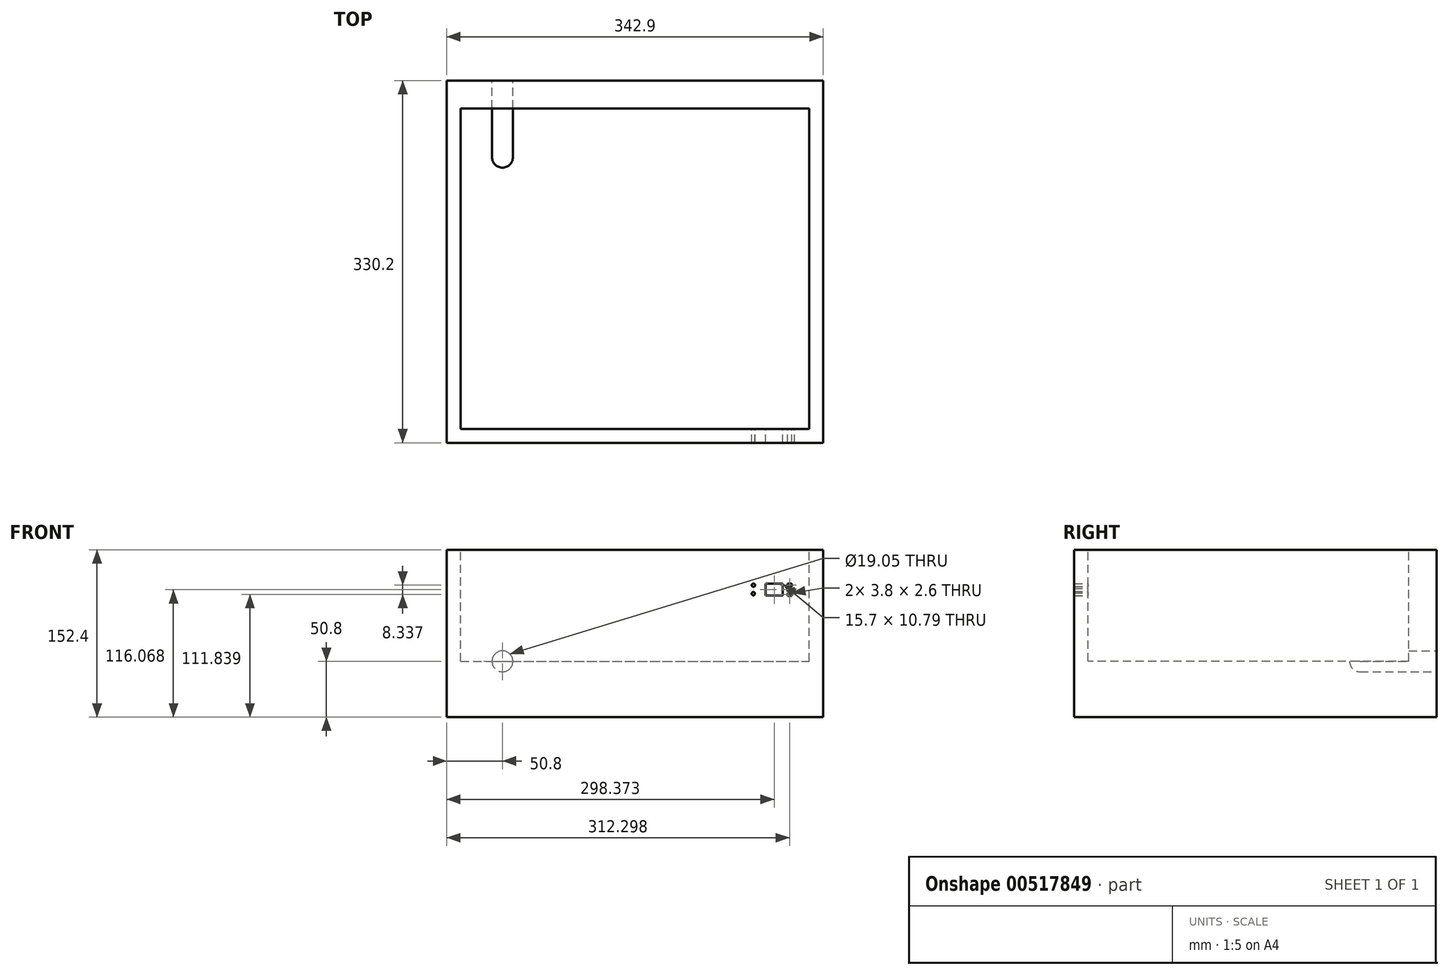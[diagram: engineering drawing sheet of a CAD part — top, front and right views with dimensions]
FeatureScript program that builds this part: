
annotation { "Feature Type Name" : "Feature", "Feature Type Description" : "" }
export const myFeature = defineFeature(function(context is Context, id is Id, definition is map)
    precondition{}
    {
        {
            var Q0;
            Q0=qCreatedBy(makeId("Top.planeOp"),FACE);
            var sketch = newSketch(context, id + "F0", { "sketchPlane" : qUnion([Q0])});
            skLineSegment(sketch, "E0.bottom", {"start": v(171.45, -165.1) * mm, "end": v(-171.45, -165.1) * mm});
            skLineSegment(sketch, "E0.top", {"start": v(171.45, 165.1) * mm, "end": v(-171.45, 165.1) * mm});
            skLineSegment(sketch, "E0.left", {"start": v(171.45, -165.1) * mm, "end": v(171.45, 165.1) * mm});
            skLineSegment(sketch, "E0.right", {"start": v(-171.45, -165.1) * mm, "end": v(-171.45, 165.1) * mm});
            skPoint(sketch, "E0.middle", {"position": v(0, 0) * mm});
            skSolve(sketch);
        }
        {
            var Q0;
            Q0 = qSketchRegion(id + "F0", true);
            extrude(context, id + "F1", {"entities" : qUnion([Q0]), "depth" : 152.4 * mm, "offsetDistance" : 25.4 * mm});
        }
        {
            var Q0;
            Q0=makeQuery(id+"F1.opExtrude","CAP_FACE",FACE,{"disambiguationData":[OSD([sQuery(id+"F0.wireOp",EDGE,"E0.bottom"),sQuery(id+"F0.wireOp",EDGE,"E0.top"),sQuery(id+"F0.wireOp",EDGE,"E0.left"),sQuery(id+"F0.wireOp",EDGE,"E0.right")])],"isStart":false});
            var sketch = newSketch(context, id + "F2", { "sketchPlane" : qUnion([Q0])});
            skLineSegment(sketch, "E1.bottom", {"start": v(-158.75, 139.7) * mm, "end": v(158.75, 139.7) * mm});
            skLineSegment(sketch, "E1.top", {"start": v(-158.75, -152.4) * mm, "end": v(158.75, -152.4) * mm});
            skLineSegment(sketch, "E1.left", {"start": v(-158.75, 139.7) * mm, "end": v(-158.75, -152.4) * mm});
            skLineSegment(sketch, "E1.right", {"start": v(158.75, 139.7) * mm, "end": v(158.75, -152.4) * mm});
            skSolve(sketch);
        }
        {
            var Q0;
            Q0 = qSketchRegion(id + "F2", true);
            extrude(context, id + "F3", {"entities" : qUnion([Q0]), "operationType" : NewBodyOperationType.REMOVE, "oppositeDirection" : true, "depth" : 101.6 * mm, "offsetDistance" : 25.4 * mm});
        }
        {
            var Q0;
            Q0=makeQuery(id+"F1.opExtrude","SWEPT_FACE",FACE,{"disambiguationData":[OSD([sQuery(id+"F0.wireOp",EDGE,"E0.top")])]});
            var sketch = newSketch(context, id + "F4", { "sketchPlane" : qUnion([Q0])});
            skCircle(sketch, "E2", {"center": v(120.65, 50.8) * mm, "radius": 9.53 * mm});
            skSolve(sketch);
        }
        {
            var Q0;
            Q0=makeQuery(id+"F4.imprint","IMPRINT",FACE,{"disambiguationData":[TD([[makeQuery(id+"F4.imprint","IMPRINT",EDGE,{"derivedFrom":sQuery(id+"F4.wireOp",EDGE,"E2")}),1.0]])]});
            extrude(context, id + "F5", {"entities" : qUnion([Q0]), "operationType" : NewBodyOperationType.REMOVE, "endBound" : BoundingType.SYMMETRIC, "oppositeDirection" : true, "depth" : 139.7 * mm, "offsetDistance" : 25.4 * mm});
        }
        {
            var Q0;
            Q0=makeQuery(id+"F3.boolean.opBoolean","COPY",FACE,{"derivedFrom":makeQuery(id+"F3.opExtrude","CAP_FACE",FACE,{"disambiguationData":[OSD([sQuery(id+"F2.wireOp",EDGE,"E1.bottom"),sQuery(id+"F2.wireOp",EDGE,"E1.top"),sQuery(id+"F2.wireOp",EDGE,"E1.left"),sQuery(id+"F2.wireOp",EDGE,"E1.right")])],"isStart":false})});
            var sketch = newSketch(context, id + "F6", { "sketchPlane" : qUnion([Q0])});
            skArc(sketch, "E3", {"start": v(-130.17, 95.25) * mm, "mid": v(-120.65, 85.73) * mm, "end": v(-111.13, 95.25) * mm});
            skSolve(sketch);
        }
        {
            var Q0;
            Q0=makeQuery(id+"F6.imprint","IMPRINT",FACE,{"disambiguationData":[TD([[makeQuery(id+"F6.imprint","IMPRINT",EDGE,{"derivedFrom":sQuery(id+"F6.wireOp",EDGE,"E3")}),1.0]])]});
            var Q1;
            Q1=makeQuery(id+"F5.boolean.opBoolean","INTERSECT",EDGE,{"derivedFrom":[makeQuery(id+"F3.boolean.opBoolean","COPY",FACE,{"derivedFrom":makeQuery(id+"F3.opExtrude","CAP_FACE",FACE,{"disambiguationData":[OSD([sQuery(id+"F2.wireOp",EDGE,"E1.bottom"),sQuery(id+"F2.wireOp",EDGE,"E1.top"),sQuery(id+"F2.wireOp",EDGE,"E1.left"),sQuery(id+"F2.wireOp",EDGE,"E1.right")])],"isStart":false})}),makeQuery(id+"F5.opExtrude","CAP_FACE",FACE,{"disambiguationData":[OSD([sQuery(id+"F4.wireOp",EDGE,"E2")])],"isStart":false})]});
            revolve(context, id + "F7", {"operationType" : NewBodyOperationType.REMOVE, "entities" : qUnion([Q0]), "axis" : qUnion([Q1]), "revolveType" : RevolveType.FULL, "oppositeDirection" : true});
        }
        {
            var Q0;
            Q0=makeQuery(id+"F3.boolean.opBoolean","COPY",FACE,{"derivedFrom":makeQuery(id+"F3.opExtrude","SWEPT_FACE",FACE,{"disambiguationData":[OSD([sQuery(id+"F2.wireOp",EDGE,"E1.top")])]})});
            var sketch = newSketch(context, id + "F8", { "sketchPlane" : qUnion([Q0])});
            skCircle(sketch, "E4", {"center": v(-107.87, 112.41) * mm, "radius": 1.5 * mm});
            skCircle(sketch, "E5", {"center": v(-107.93, 120.15) * mm, "radius": 1.5 * mm});
            skLineSegment(sketch, "E6.bottom", {"start": v(-119.07, 110.67) * mm, "end": v(-134.77, 110.67) * mm});
            skLineSegment(sketch, "E6.top", {"start": v(-119.07, 121.46) * mm, "end": v(-134.77, 121.46) * mm});
            skLineSegment(sketch, "E6.left", {"start": v(-119.07, 110.67) * mm, "end": v(-119.07, 121.46) * mm});
            skLineSegment(sketch, "E6.right", {"start": v(-134.77, 110.67) * mm, "end": v(-134.77, 121.46) * mm});
            skPoint(sketch, "E6.middle", {"position": v(-126.92, 116.07) * mm});
            skLineSegment(sketch, "E7.bottom", {"start": v(-142.75, 118.88) * mm, "end": v(-138.95, 118.88) * mm});
            skLineSegment(sketch, "E7.top", {"start": v(-142.75, 121.48) * mm, "end": v(-138.95, 121.48) * mm});
            skLineSegment(sketch, "E7.left", {"start": v(-142.75, 118.88) * mm, "end": v(-142.75, 121.48) * mm});
            skLineSegment(sketch, "E7.right", {"start": v(-138.95, 118.88) * mm, "end": v(-138.95, 121.48) * mm});
            skPoint(sketch, "E7.middle", {"position": v(-140.85, 120.18) * mm});
            skLineSegment(sketch, "E8.bottom", {"start": v(-145.43, 114.57) * mm, "end": v(-139.02, 114.57) * mm});
            skLineSegment(sketch, "E8.top", {"start": v(-145.43, 117.17) * mm, "end": v(-139.02, 117.17) * mm});
            skLineSegment(sketch, "E8.left", {"start": v(-145.43, 114.57) * mm, "end": v(-145.43, 117.17) * mm});
            skLineSegment(sketch, "E8.right", {"start": v(-139.02, 114.57) * mm, "end": v(-139.02, 117.17) * mm});
            skPoint(sketch, "E8.middle", {"position": v(-142.23, 115.87) * mm});
            skLineSegment(sketch, "E9.bottom", {"start": v(-142.75, 110.54) * mm, "end": v(-138.95, 110.54) * mm});
            skLineSegment(sketch, "E9.top", {"start": v(-142.75, 113.14) * mm, "end": v(-138.95, 113.14) * mm});
            skLineSegment(sketch, "E9.left", {"start": v(-142.75, 110.54) * mm, "end": v(-142.75, 113.14) * mm});
            skLineSegment(sketch, "E9.right", {"start": v(-138.95, 110.54) * mm, "end": v(-138.95, 113.14) * mm});
            skPoint(sketch, "E9.middle", {"position": v(-140.85, 111.84) * mm});
            skSolve(sketch);
        }
        {
            var Q0;
            Q0 = qSketchRegion(id + "F8", true);
            extrude(context, id + "F9", {"entities" : qUnion([Q0]), "operationType" : NewBodyOperationType.REMOVE, "oppositeDirection" : true, "depth" : 25.4 * mm, "offsetDistance" : 25.4 * mm});
        }
    });
